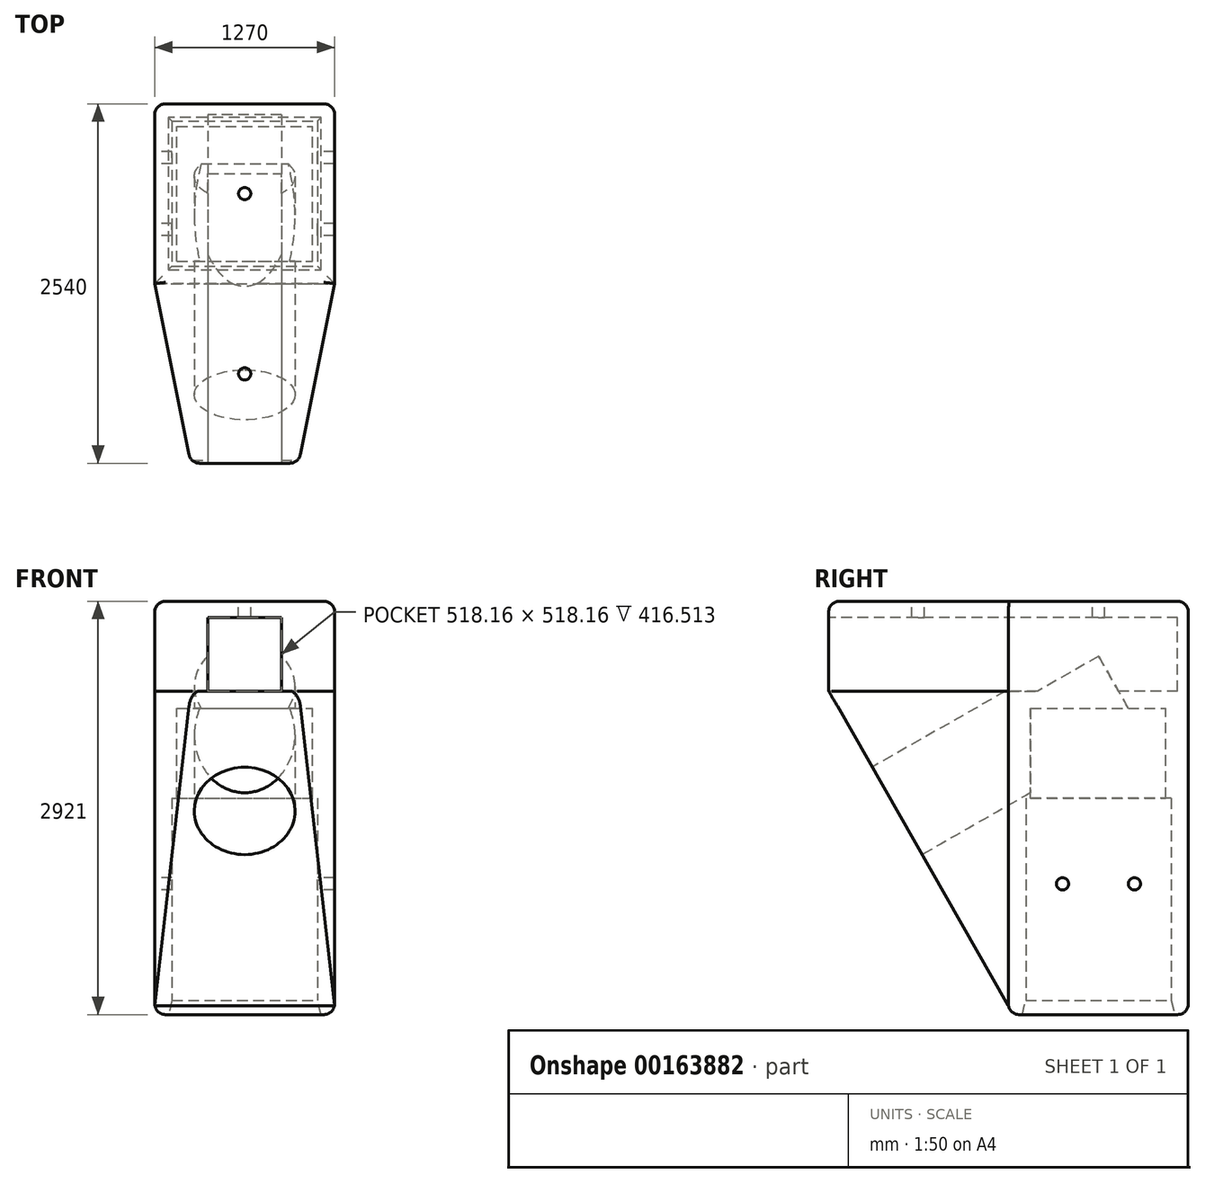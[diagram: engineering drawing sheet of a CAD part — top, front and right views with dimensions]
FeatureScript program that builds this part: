
annotation { "Feature Type Name" : "Feature", "Feature Type Description" : "" }
export const myFeature = defineFeature(function(context is Context, id is Id, definition is map)
    precondition{}
    {
        {
            var Q0;
            Q0=qCreatedBy(makeId("Top.planeOp"),FACE);
            var sketch = newSketch(context, id + "F0", { "sketchPlane" : qUnion([Q0])});
            skLineSegment(sketch, "E0.bottom", {"start": v(-635, 635) * mm, "end": v(635, 635) * mm});
            skLineSegment(sketch, "E0.top", {"start": v(-635, -635) * mm, "end": v(635, -635) * mm});
            skLineSegment(sketch, "E0.left", {"start": v(-635, 635) * mm, "end": v(-635, -635) * mm});
            skLineSegment(sketch, "E0.right", {"start": v(635, 635) * mm, "end": v(635, -635) * mm});
            skSolve(sketch);
        }
        {
            var Q0;
            Q0=makeQuery(id+"F0.imprint","IMPRINT",FACE,{"disambiguationData":[TD([[makeQuery(id+"F0.imprint","IMPRINT",EDGE,{"derivedFrom":sQuery(id+"F0.wireOp",EDGE,"E0.bottom")}),-1.0]])]});
            extrude(context, id + "F1", {"entities" : qUnion([Q0]), "depth" : 2286 * mm});
        }
        {
            var Q0;
            Q0=makeQuery(id+"F1.opExtrude","CAP_FACE",FACE,{"disambiguationData":[OSD([sQuery(id+"F0.wireOp",EDGE,"E0.bottom"),sQuery(id+"F0.wireOp",EDGE,"E0.top"),sQuery(id+"F0.wireOp",EDGE,"E0.left"),sQuery(id+"F0.wireOp",EDGE,"E0.right")])],"isStart":true});
            shell(context, id + "F2", {"entities" : qUnion([Q0]), "thickness" : 121.92 * mm});
        }
        {
            var Q0;
            Q0=makeQuery(id+"F1.opExtrude","CAP_FACE",FACE,{"disambiguationData":[OSD([sQuery(id+"F0.wireOp",EDGE,"E0.bottom"),sQuery(id+"F0.wireOp",EDGE,"E0.top"),sQuery(id+"F0.wireOp",EDGE,"E0.left"),sQuery(id+"F0.wireOp",EDGE,"E0.right")])],"isStart":false});
            var sketch = newSketch(context, id + "F3", { "sketchPlane" : qUnion([Q0])});
            skLineSegment(sketch, "E1.bottom", {"start": v(635, -635) * mm, "end": v(-635, -635) * mm});
            skLineSegment(sketch, "E1.top", {"start": v(635, 635) * mm, "end": v(-635, 635) * mm});
            skLineSegment(sketch, "E1.left", {"start": v(635, -635) * mm, "end": v(635, 635) * mm});
            skLineSegment(sketch, "E1.right", {"start": v(-635, -635) * mm, "end": v(-635, 635) * mm});
            skLineSegment(sketch, "E2.top", {"start": v(635, -1905) * mm, "end": v(-635, -1905) * mm});
            skLineSegment(sketch, "E2.left", {"start": v(635, -635) * mm, "end": v(635, -1905) * mm});
            skLineSegment(sketch, "E2.right", {"start": v(-635, -635) * mm, "end": v(-635, -1905) * mm});
            skSolve(sketch);
        }
        {
            var Q0;
            Q0=makeQuery(id+"F3.imprint","IMPRINT",FACE,{"disambiguationData":[TD([[makeQuery(id+"F3.imprint","IMPRINT",EDGE,{"derivedFrom":sQuery(id+"F3.wireOp",EDGE,"E1.top")}),-1.0]])]});
            var Q1;
            Q1=makeQuery(id+"F3.imprint","IMPRINT",FACE,{"disambiguationData":[TD([[makeQuery(id+"F3.imprint","IMPRINT",EDGE,{"derivedFrom":sQuery(id+"F3.wireOp",EDGE,"E1.bottom")}),-1.0]])]});
            extrude(context, id + "F4", {"entities" : qUnion([Q0, Q1]), "operationType" : NewBodyOperationType.ADD, "depth" : 635 * mm});
        }
        {
            var Q0;
            Q0=qCreatedBy(makeId("Right.planeOp"),FACE);
            var sketch = newSketch(context, id + "F5", { "sketchPlane" : qUnion([Q0])});
            skLineSegment(sketch, "E3", {"start": v(-1904.98, 2286) * mm, "end": v(-633.9, 59.18) * mm});
            skLineSegment(sketch, "E4", {"start": v(-633.9, 59.18) * mm, "end": v(-633.9, 2285.62) * mm});
            skLineSegment(sketch, "E5", {"start": v(-633.9, 2285.62) * mm, "end": v(-1904.98, 2286) * mm});
            skSolve(sketch);
        }
        {
            var Q0;
            Q0=makeQuery(id+"F5.imprint","IMPRINT",FACE,{"disambiguationData":[TD([[makeQuery(id+"F5.imprint","IMPRINT",EDGE,{"derivedFrom":sQuery(id+"F5.wireOp",EDGE,"E3")}),1.0]])]});
            extrude(context, id + "F6", {"entities" : qUnion([Q0]), "operationType" : NewBodyOperationType.ADD, "depth" : 635 * mm, "hasSecondDirection" : true, "secondDirectionOppositeDirection" : true, "secondDirectionDepth" : 635 * mm});
        }
        {
            var Q0;
            Q0=makeQuery(id+"F4.opExtrude","SWEPT_FACE",FACE,{"disambiguationData":[OSD([sQuery(id+"F3.wireOp",EDGE,"E2.top")])]});
            var sketch = newSketch(context, id + "F7", { "sketchPlane" : qUnion([Q0])});
            skLineSegment(sketch, "E6.bottom", {"start": v(-259.08, 2286) * mm, "end": v(259.08, 2286) * mm});
            skLineSegment(sketch, "E6.top", {"start": v(-259.08, 2804.16) * mm, "end": v(259.08, 2804.16) * mm});
            skLineSegment(sketch, "E6.left", {"start": v(-259.08, 2286) * mm, "end": v(-259.08, 2804.16) * mm});
            skLineSegment(sketch, "E6.right", {"start": v(259.08, 2286) * mm, "end": v(259.08, 2804.16) * mm});
            skSolve(sketch);
        }
        {
            var Q0;
            Q0=makeQuery(id+"F7.imprint","IMPRINT",FACE,{"disambiguationData":[TD([[makeQuery(id+"F7.imprint","IMPRINT",EDGE,{"derivedFrom":sQuery(id+"F7.wireOp",EDGE,"E6.bottom")}),-1.0]])]});
            extrude(context, id + "F8", {"entities" : qUnion([Q0]), "operationType" : NewBodyOperationType.REMOVE, "oppositeDirection" : true, "depth" : 2463.8 * mm});
        }
        {
            var Q0;
            Q0=makeQuery(id+"F4.opExtrude","SWEPT_EDGE",EDGE,{"disambiguationData":[OSD([sQuery(id+"F3.wireOp",EDGE,"E2.top"),sQuery(id+"F3.wireOp",EDGE,"E2.right")])]});
            var Q1;
            Q1=makeQuery(id+"F4.opExtrude","SWEPT_EDGE",EDGE,{"disambiguationData":[OSD([sQuery(id+"F3.wireOp",EDGE,"E2.top"),sQuery(id+"F3.wireOp",EDGE,"E2.left")])]});
            chamfer(context, id + "F9", {"entities" : qUnion([Q0, Q1]), "chamferType" : ChamferType.TWO_OFFSETS, "width1" : 254 * mm, "oppositeDirection" : false, "width2" : 1270 * mm, "tangentPropagation" : true});
        }
        {
            var Q0;
            Q0=makeQuery(id+"F4.opExtrude","CAP_FACE",FACE,{"disambiguationData":[OSD([sQuery(id+"F3.wireOp",EDGE,"E1.top"),sQuery(id+"F3.wireOp",EDGE,"E1.left"),sQuery(id+"F3.wireOp",EDGE,"E1.right"),sQuery(id+"F3.wireOp",EDGE,"E2.top"),sQuery(id+"F3.wireOp",EDGE,"E2.left"),sQuery(id+"F3.wireOp",EDGE,"E2.right")])],"isStart":false});
            var sketch = newSketch(context, id + "F10", { "sketchPlane" : qUnion([Q0])});
            skCircle(sketch, "E7", {"center": v(0, -1273.88) * mm, "radius": 43.18 * mm});
            skCircle(sketch, "E8", {"center": v(0, 0) * mm, "radius": 43.18 * mm});
            skSolve(sketch);
        }
        {
            var Q0;
            Q0=makeQuery(id+"F10.imprint","IMPRINT",FACE,{"disambiguationData":[TD([[makeQuery(id+"F10.imprint","IMPRINT",EDGE,{"derivedFrom":sQuery(id+"F10.wireOp",EDGE,"E8")}),1.0]])]});
            extrude(context, id + "F11", {"entities" : qUnion([Q0]), "operationType" : NewBodyOperationType.REMOVE, "endBound" : BoundingType.THROUGH_ALL, "oppositeDirection" : true, "depth" : 25.4 * mm});
        }
        {
            var Q0;
            Q0=makeQuery(id+"F10.imprint","IMPRINT",FACE,{"disambiguationData":[TD([[makeQuery(id+"F10.imprint","IMPRINT",EDGE,{"derivedFrom":sQuery(id+"F10.wireOp",EDGE,"E7")}),1.0]])]});
            extrude(context, id + "F12", {"entities" : qUnion([Q0]), "operationType" : NewBodyOperationType.REMOVE, "oppositeDirection" : true, "depth" : 254 * mm});
        }
        {
            var Q0;
            Q0=makeQuery(id+"F4.boolean.opBoolean","MERGE",FACE,{"derivedFrom":[makeQuery(id+"F1.opExtrude","SWEPT_FACE",FACE,{"disambiguationData":[OSD([sQuery(id+"F0.wireOp",EDGE,"E0.left")])]}),makeQuery(id+"F4.opExtrude","SWEPT_FACE",FACE,{"disambiguationData":[OSD([sQuery(id+"F3.wireOp",EDGE,"E1.right"),sQuery(id+"F3.wireOp",EDGE,"E2.right")])]})]});
            var sketch = newSketch(context, id + "F13", { "sketchPlane" : qUnion([Q0])});
            skCircle(sketch, "E9", {"center": v(-254, 924.06) * mm, "radius": 43.18 * mm});
            skCircle(sketch, "E10", {"center": v(254, 924.06) * mm, "radius": 43.18 * mm});
            skSolve(sketch);
        }
        {
            var Q0;
            Q0=makeQuery(id+"F13.imprint","IMPRINT",FACE,{"disambiguationData":[TD([[makeQuery(id+"F13.imprint","IMPRINT",EDGE,{"derivedFrom":sQuery(id+"F13.wireOp",EDGE,"E9")}),1.0]])]});
            var Q1;
            Q1=makeQuery(id+"F13.imprint","IMPRINT",FACE,{"disambiguationData":[TD([[makeQuery(id+"F13.imprint","IMPRINT",EDGE,{"derivedFrom":sQuery(id+"F13.wireOp",EDGE,"E10")}),1.0]])]});
            extrude(context, id + "F14", {"entities" : qUnion([Q0, Q1]), "operationType" : NewBodyOperationType.REMOVE, "endBound" : BoundingType.THROUGH_ALL, "oppositeDirection" : true, "depth" : 25.4 * mm});
        }
        {
            var Q0;
            {var subQ0=sQuery(id+"F3.wireOp",EDGE,"E2.left");var subQ1=sQuery(id+"F3.wireOp",EDGE,"E2.top");Q0=makeQuery(id+"F9.opChamfer","BLEND_EDGE",EDGE,{"blendedFrom":[makeQuery(id+"F4.opExtrude","SWEPT_EDGE",EDGE,{"disambiguationData":[OSD([subQ1,subQ0])]}),makeQuery(id+"F4.opExtrude","CAP_FACE",FACE,{"disambiguationData":[OSD([sQuery(id+"F3.wireOp",EDGE,"E1.top"),sQuery(id+"F3.wireOp",EDGE,"E1.left"),sQuery(id+"F3.wireOp",EDGE,"E1.right"),subQ1,subQ0,sQuery(id+"F3.wireOp",EDGE,"E2.right")])],"isStart":false})],"blendedInto":[makeQuery(id+"F4.opExtrude","CAP_FACE",FACE,{"disambiguationData":[OSD([sQuery(id+"F3.wireOp",EDGE,"E1.top"),sQuery(id+"F3.wireOp",EDGE,"E1.left"),sQuery(id+"F3.wireOp",EDGE,"E1.right"),subQ1,subQ0,sQuery(id+"F3.wireOp",EDGE,"E2.right")])],"isStart":false})]});}
            var Q1;
            Q1=makeQuery(id+"F4.opExtrude","CAP_EDGE",EDGE,{"disambiguationData":[OSD([sQuery(id+"F3.wireOp",EDGE,"E2.top")])],"isStart":false});
            var Q2;
            {var subQ0=sQuery(id+"F3.wireOp",EDGE,"E2.right");var subQ1=sQuery(id+"F3.wireOp",EDGE,"E2.top");Q2=makeQuery(id+"F9.opChamfer","BLEND_EDGE",EDGE,{"blendedFrom":[makeQuery(id+"F4.opExtrude","SWEPT_EDGE",EDGE,{"disambiguationData":[OSD([subQ1,subQ0])]}),makeQuery(id+"F4.opExtrude","CAP_FACE",FACE,{"disambiguationData":[OSD([sQuery(id+"F3.wireOp",EDGE,"E1.top"),sQuery(id+"F3.wireOp",EDGE,"E1.left"),sQuery(id+"F3.wireOp",EDGE,"E1.right"),subQ1,sQuery(id+"F3.wireOp",EDGE,"E2.left"),subQ0])],"isStart":false})],"blendedInto":[makeQuery(id+"F4.opExtrude","CAP_FACE",FACE,{"disambiguationData":[OSD([sQuery(id+"F3.wireOp",EDGE,"E1.top"),sQuery(id+"F3.wireOp",EDGE,"E1.left"),sQuery(id+"F3.wireOp",EDGE,"E1.right"),subQ1,sQuery(id+"F3.wireOp",EDGE,"E2.left"),subQ0])],"isStart":false})]});}
            var Q3;
            Q3=makeQuery(id+"F4.opExtrude","CAP_EDGE",EDGE,{"disambiguationData":[OSD([sQuery(id+"F3.wireOp",EDGE,"E1.right"),sQuery(id+"F3.wireOp",EDGE,"E2.right")])],"isStart":false});
            var Q4;
            Q4=makeQuery(id+"F4.opExtrude","CAP_EDGE",EDGE,{"disambiguationData":[OSD([sQuery(id+"F3.wireOp",EDGE,"E1.top")])],"isStart":false});
            var Q5;
            Q5=makeQuery(id+"F4.opExtrude","CAP_EDGE",EDGE,{"disambiguationData":[OSD([sQuery(id+"F3.wireOp",EDGE,"E1.left"),sQuery(id+"F3.wireOp",EDGE,"E2.left")])],"isStart":false});
            var Q6;
            Q6=makeQuery(id+"F4.boolean.opBoolean","MERGE",EDGE,{"derivedFrom":[makeQuery(id+"F1.opExtrude","SWEPT_EDGE",EDGE,{"disambiguationData":[OSD([sQuery(id+"F0.wireOp",EDGE,"E0.bottom"),sQuery(id+"F0.wireOp",EDGE,"E0.right")])]}),makeQuery(id+"F4.opExtrude","SWEPT_EDGE",EDGE,{"disambiguationData":[OSD([sQuery(id+"F3.wireOp",EDGE,"E1.top"),sQuery(id+"F3.wireOp",EDGE,"E1.left")])]})]});
            var Q7;
            Q7=makeQuery(id+"F4.boolean.opBoolean","MERGE",EDGE,{"derivedFrom":[makeQuery(id+"F1.opExtrude","SWEPT_EDGE",EDGE,{"disambiguationData":[OSD([sQuery(id+"F0.wireOp",EDGE,"E0.bottom"),sQuery(id+"F0.wireOp",EDGE,"E0.left")])]}),makeQuery(id+"F4.opExtrude","SWEPT_EDGE",EDGE,{"disambiguationData":[OSD([sQuery(id+"F3.wireOp",EDGE,"E1.top"),sQuery(id+"F3.wireOp",EDGE,"E1.right")])]})]});
            var Q8;
            Q8=makeQuery(id+"F6.opExtrude","CAP_EDGE",EDGE,{"disambiguationData":[OSD([sQuery(id+"F5.wireOp",EDGE,"E3")])],"isStart":false});
            var Q9;
            Q9=makeQuery(id+"F6.opExtrude","CAP_EDGE",EDGE,{"disambiguationData":[OSD([sQuery(id+"F5.wireOp",EDGE,"E3")])],"isStart":true});
            var Q10;
            Q10=makeQuery(id+"F1.opExtrude","CAP_EDGE",EDGE,{"disambiguationData":[OSD([sQuery(id+"F0.wireOp",EDGE,"E0.bottom")])],"isStart":true});
            var Q11;
            Q11=makeQuery(id+"F1.opExtrude","CAP_EDGE",EDGE,{"disambiguationData":[OSD([sQuery(id+"F0.wireOp",EDGE,"E0.right")])],"isStart":true});
            var Q12;
            Q12=makeQuery(id+"F1.opExtrude","CAP_EDGE",EDGE,{"disambiguationData":[OSD([sQuery(id+"F0.wireOp",EDGE,"E0.left")])],"isStart":true});
            fillet(context, id + "F15", {"entities" : qUnion([Q0, Q1, Q2, Q3, Q4, Q5, Q6, Q7, Q8, Q9, Q10, Q11, Q12]), "radius" : 76.2 * mm, "tangentPropagation" : true, "allowEdgeOverflow" : false});
        }
        {
            var Q0;
            {var subQ0=sQuery(id+"F0.wireOp",EDGE,"E0.left");Q0=makeQuery(id+"F2.opShell","OFFSET_EDGE",EDGE,{"disambiguationData":[OSD([subQ0]),TDD([makeQuery(id+"F1.opExtrude","CAP_EDGE",EDGE,{"disambiguationData":[OSD([subQ0])],"isStart":true})])]});}
            var Q1;
            {var subQ0=sQuery(id+"F0.wireOp",EDGE,"E0.top");Q1=makeQuery(id+"F2.opShell","OFFSET_EDGE",EDGE,{"disambiguationData":[OSD([subQ0]),TDD([makeQuery(id+"F1.opExtrude","CAP_EDGE",EDGE,{"disambiguationData":[OSD([subQ0])],"isStart":true})])]});}
            var Q2;
            {var subQ0=sQuery(id+"F0.wireOp",EDGE,"E0.right");Q2=makeQuery(id+"F2.opShell","OFFSET_EDGE",EDGE,{"disambiguationData":[OSD([subQ0]),TDD([makeQuery(id+"F1.opExtrude","CAP_EDGE",EDGE,{"disambiguationData":[OSD([subQ0])],"isStart":true})])]});}
            var Q3;
            {var subQ0=sQuery(id+"F0.wireOp",EDGE,"E0.bottom");Q3=makeQuery(id+"F2.opShell","OFFSET_EDGE",EDGE,{"disambiguationData":[OSD([subQ0]),TDD([makeQuery(id+"F1.opExtrude","CAP_EDGE",EDGE,{"disambiguationData":[OSD([subQ0])],"isStart":true})])]});}
            chamfer(context, id + "F16", {"entities" : qUnion([Q0, Q1, Q2, Q3]), "chamferType" : ChamferType.TWO_OFFSETS, "width1" : 25.4 * mm, "oppositeDirection" : false, "width2" : 101.6 * mm, "tangentPropagation" : true});
        }
        {
            var Q0;
            Q0=makeQuery(id+"F2.opShell","OFFSET_FACE",FACE,{"disambiguationData":[OSD([sQuery(id+"F0.wireOp",EDGE,"E0.bottom"),sQuery(id+"F0.wireOp",EDGE,"E0.top"),sQuery(id+"F0.wireOp",EDGE,"E0.left"),sQuery(id+"F0.wireOp",EDGE,"E0.right")])]});
            var sketch = newSketch(context, id + "F17", { "sketchPlane" : qUnion([Q0])});
            skLineSegment(sketch, "E11.bottom", {"start": v(-513.08, 513.08) * mm, "end": v(513.08, 513.08) * mm});
            skLineSegment(sketch, "E11.top", {"start": v(-513.08, -513.08) * mm, "end": v(513.08, -513.08) * mm});
            skLineSegment(sketch, "E11.left", {"start": v(-513.08, 513.08) * mm, "end": v(-513.08, -513.08) * mm});
            skLineSegment(sketch, "E11.right", {"start": v(513.08, 513.08) * mm, "end": v(513.08, -513.08) * mm});
            skLineSegment(sketch, "E12.bottom", {"start": v(-479.73, 479.28) * mm, "end": v(477.93, 479.28) * mm});
            skLineSegment(sketch, "E12.top", {"start": v(-479.73, -475.64) * mm, "end": v(477.93, -475.64) * mm});
            skLineSegment(sketch, "E12.left", {"start": v(-479.73, 479.28) * mm, "end": v(-479.73, -475.64) * mm});
            skLineSegment(sketch, "E12.right", {"start": v(477.93, 479.28) * mm, "end": v(477.93, -475.64) * mm});
            skSolve(sketch);
        }
        {
            var Q0;
            Q0=makeQuery(id+"F6.opExtrude","SWEPT_FACE",FACE,{"disambiguationData":[OSD([sQuery(id+"F5.wireOp",EDGE,"E3")])]});
            var sketch = newSketch(context, id + "F18", { "sketchPlane" : qUnion([Q0])});
            skCircle(sketch, "E13", {"center": v(0, 1954.88) * mm, "radius": 355.6 * mm});
            skSolve(sketch);
        }
        {
            var Q0;
            Q0=makeQuery(id+"F17.imprint","IMPRINT",FACE,{"disambiguationData":[TD([[makeQuery(id+"F17.imprint","IMPRINT",EDGE,{"derivedFrom":sQuery(id+"F17.wireOp",EDGE,"E11.bottom")}),-1.0]])]});
            extrude(context, id + "F19", {"entities" : qUnion([Q0]), "operationType" : NewBodyOperationType.ADD, "depth" : 635 * mm});
        }
        {
            var Q0;
            Q0=makeQuery(id+"F18.imprint","IMPRINT",FACE,{"disambiguationData":[TD([[makeQuery(id+"F18.imprint","IMPRINT",EDGE,{"derivedFrom":sQuery(id+"F18.wireOp",EDGE,"E13")}),1.0]])]});
            extrude(context, id + "F20", {"entities" : qUnion([Q0]), "operationType" : NewBodyOperationType.REMOVE, "oppositeDirection" : true, "depth" : 1778 * mm});
        }
        {
            var Q0;
            Q0=makeQuery(id+"F1.opExtrude","CAP_EDGE",EDGE,{"disambiguationData":[OSD([sQuery(id+"F0.wireOp",EDGE,"E0.top")])],"isStart":true});
            var Q1;
            Q1=makeQuery(id+"F20.boolean.opBoolean","COPY",EDGE,{"derivedFrom":makeQuery(id+"F20.opExtrude","CAP_EDGE",EDGE,{"disambiguationData":[OSD([sQuery(id+"F18.wireOp",EDGE,"E13")])],"isStart":true})});
            fillet(context, id + "F21", {"entities" : qUnion([Q0, Q1]), "radius" : 76.2 * mm, "tangentPropagation" : true, "allowEdgeOverflow" : false});
        }
        {
            var Q0;
            {var subQ0=sQuery(id+"F3.wireOp",EDGE,"E2.top");Q0=makeQuery(id+"F9.opChamfer","BLEND_EDGE",EDGE,{"blendedFrom":[makeQuery(id+"F4.opExtrude","SWEPT_EDGE",EDGE,{"disambiguationData":[OSD([subQ0,sQuery(id+"F3.wireOp",EDGE,"E2.left")])]}),makeQuery(id+"F4.opExtrude","SWEPT_FACE",FACE,{"disambiguationData":[OSD([subQ0])]})],"blendedInto":[makeQuery(id+"F4.opExtrude","SWEPT_FACE",FACE,{"disambiguationData":[OSD([subQ0])]})]});}
            var Q1;
            {var subQ0=sQuery(id+"F3.wireOp",EDGE,"E2.top");Q1=makeQuery(id+"F9.opChamfer","BLEND_EDGE",EDGE,{"blendedFrom":[makeQuery(id+"F4.opExtrude","SWEPT_EDGE",EDGE,{"disambiguationData":[OSD([subQ0,sQuery(id+"F3.wireOp",EDGE,"E2.right")])]}),makeQuery(id+"F4.opExtrude","SWEPT_FACE",FACE,{"disambiguationData":[OSD([subQ0])]})],"blendedInto":[makeQuery(id+"F4.opExtrude","SWEPT_FACE",FACE,{"disambiguationData":[OSD([subQ0])]})]});}
            fillet(context, id + "F22", {"entities" : qUnion([Q0, Q1]), "radius" : 76.2 * mm, "tangentPropagation" : true, "allowEdgeOverflow" : false});
        }
    });
